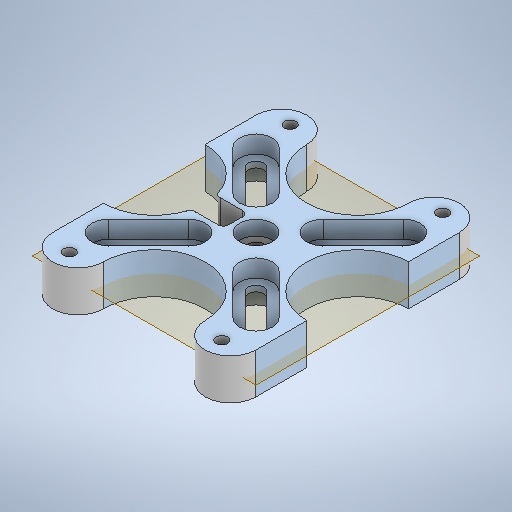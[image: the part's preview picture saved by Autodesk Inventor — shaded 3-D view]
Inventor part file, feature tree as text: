
AUTODESK INVENTOR PART (.ipt)
format: ipt  version: 2025.1 (Build 291241000, 241)  size: 535,040 bytes
history: native  units: in
note: dims shown in document units (in); Inventor stores cm internally (conversion verified against a paired STEP export)
features: extrude x7, sketch x7, other x3, mirror x2, plane x1, fillet x1
ambient origin geometry x8: Origin, YZ Plane, XZ Plane, XY Plane, X Axis, Y Axis, Z Axis, Center Point
bodies: Solid1 (feature_tree)
feature tree (21):
  extrude  "Extrusion1"  Depth=1.0in
  plane  "Work Plane1"
  extrude  "Extrusion2"  Depth=2.0in
  extrude  "Extrusion3"  Depth=0.4429in
  extrude  "Extrusion4"  Depth=0.4429in
  extrude  "Extrusion5"  Depth=0.4429in
  mirror  "Mirror1"
  mirror  "Mirror2"
  extrude  "Extrusion6"  Depth=0.4429in
  extrude  "Extrusion7"  Depth=2.7559in
  fillet  "Fillet1"  Radius=0.2126in
  sketch  "Sketch1"  dims[d0=1.0in d1=1.0in]
  sketch  "Sketch3"  dims[d4=2.0in d5=2.0in]
  sketch  "Sketch5"  dims[d6=0.4402in d7=0.4429in]
  sketch  "Sketch7"  dims[d8=0.4429in d9=0.4429in]
  sketch  "Sketch8"  dims[d10=0.4429in d11=0.4429in]
  sketch  "Sketch9"  dims[d12=0.4429in d13=0.4429in]
  sketch  "Sketch10"  dims[d14=0.4429in d15=2.7559in d16=0.2126in d17=0.2126in d18=0.5512in d19=0.0in d36=-0.2756in d37=1.0in d38=1.0in d39=2.0in d40=2.0in d41=0.4331in d42=0.4429in d43=0.4429in d44=0.4429in d45=0.4429in d46=0.4429in d47=0.4429in d48=0.4429in d49=0.4429in d50=2.7559in d51=0.2087in d52=0.2087in d53=0.0787in d54=0.0in d79=1.378in d80=1.378in d81=1.378in d82=1.378in d83=1.2687in d84=0.0in d85=0.5512in d86=0.0in d90=0.5512in d91=0.0in d94=0.2362in d95=0.3543in d96=0.0in d97=0.1575in d100=0.5512in d101=0.0in d102=0.0787in]
  other  "Finish1"
  other  "Finish2"
  other  "Finish3"
